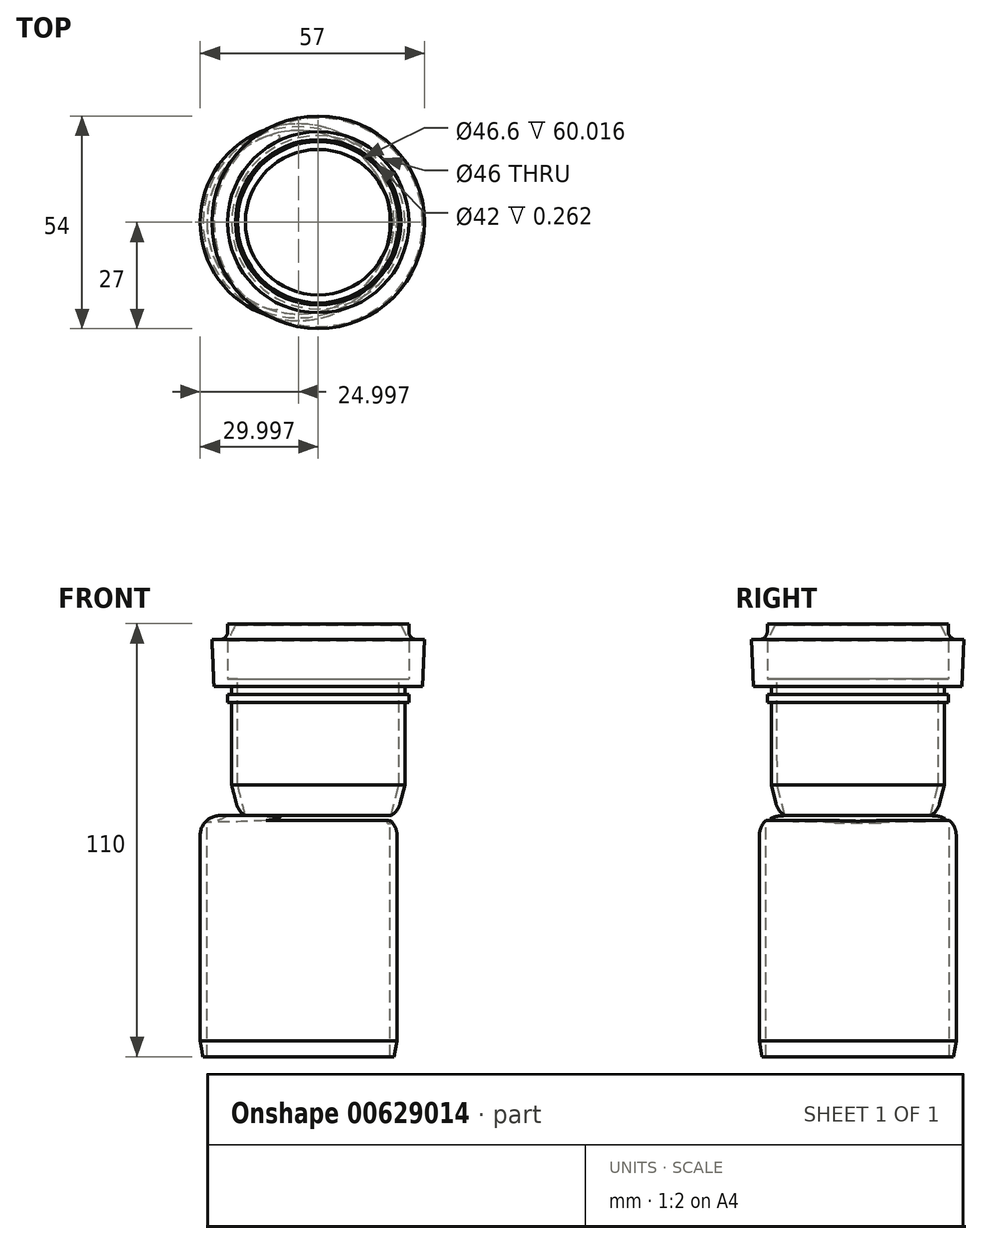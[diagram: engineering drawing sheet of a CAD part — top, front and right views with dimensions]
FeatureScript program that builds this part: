
annotation { "Feature Type Name" : "Feature", "Feature Type Description" : "" }
export const myFeature = defineFeature(function(context is Context, id is Id, definition is map)
    precondition{}
    {
        {
            var Q0;
            Q0=qCreatedBy(makeId("Front.planeOp"),FACE);
            var sketch = newSketch(context, id + "F0", { "sketchPlane" : qUnion([Q0])});
            skLineSegment(sketch, "E0", {"start": v(21.37, -67.8) * mm, "end": v(21.37, 7.5) * mm});
            skLineSegment(sketch, "E1", {"start": v(-0.63, -1.77) * mm, "end": v(-0.63, -22.77) * mm});
            skLineSegment(sketch, "E2", {"start": v(-0.63, -22.77) * mm, "end": v(1.37, -30.52) * mm});
            skLineSegment(sketch, "E3", {"start": v(-0.63, -1.77) * mm, "end": v(-1.63, -1.77) * mm});
            skLineSegment(sketch, "E4", {"start": v(-1.63, -1.77) * mm, "end": v(-1.63, 0.23) * mm});
            skLineSegment(sketch, "E5", {"start": v(-1.63, 0.23) * mm, "end": v(-0.63, 0.23) * mm});
            skLineSegment(sketch, "E6", {"start": v(-0.63, 0.23) * mm, "end": v(-0.63, 2.23) * mm});
            skLineSegment(sketch, "E7", {"start": v(-0.63, 2.23) * mm, "end": v(-5.13, 2.23) * mm});
            skLineSegment(sketch, "E8", {"start": v(-5.13, 2.23) * mm, "end": v(-5.63, 14.22) * mm});
            skLineSegment(sketch, "E9", {"start": v(-5.63, 14.22) * mm, "end": v(-3.63, 14.22) * mm});
            skLineSegment(sketch, "E10", {"start": v(-1.63, 16.22) * mm, "end": v(-1.63, 18.22) * mm});
            skLineSegment(sketch, "E11", {"start": v(-1.63, 18.22) * mm, "end": v(0.37, 18.22) * mm});
            skLineSegment(sketch, "E12", {"start": v(-1.63, 4.23) * mm, "end": v(-1.63, 13.9) * mm});
            skLineSegment(sketch, "E13", {"start": v(-1.63, 4.23) * mm, "end": v(0.87, 4.24) * mm});
            skPoint(sketch, "E14.visualSharp", {"position": v(-1.63, 14.22) * mm});
            skArc(sketch, "E14.filletArc", {"start": v(-3.63, 14.22) * mm, "mid": v(-2.22, 14.8) * mm, "end": v(-1.63, 16.22) * mm});
            skLineSegment(sketch, "E15", {"start": v(1.37, -30.52) * mm, "end": v(2.87, -30.52) * mm});
            skLineSegment(sketch, "E16", {"start": v(0.89, -22.73) * mm, "end": v(0.87, 4.24) * mm});
            skLineSegment(sketch, "E17", {"start": v(2.87, -30.52) * mm, "end": v(0.89, -22.73) * mm});
            skLineSegment(sketch, "E18", {"start": v(0.37, 18.22) * mm, "end": v(0.37, 17.95) * mm});
            skLineSegment(sketch, "E19", {"start": v(0.37, 17.95) * mm, "end": v(-1.63, 13.9) * mm});
            skSolve(sketch);
        }
        {
            var Q0;
            Q0=makeQuery(id+"F0.imprint","IMPRINT",FACE,{"disambiguationData":[TD([[makeQuery(id+"F0.imprint","IMPRINT",EDGE,{"derivedFrom":sQuery(id+"F0.wireOp",EDGE,"E1")}),1.0]])]});
            var Q1;
            Q1=sQuery(id+"F0.wireOp",EDGE,"E0");
            revolve(context, id + "F1", {"entities" : qUnion([Q0]), "axis" : qUnion([Q1]), "revolveType" : RevolveType.FULL});
        }
        {
            var Q0;
            Q0=makeQuery(id+"F1.opRevolve","SWEPT_FACE",FACE,{"disambiguationData":[OSD([sQuery(id+"F0.wireOp",EDGE,"E15")])]});
            cPlane(context, id + "F2", {"entities" : qUnion([Q0]), "cplaneType" : CPlaneType.OFFSET, "offset" : 0 * mm, "width" : 150 * mm, "height" : 150 * mm});
        }
        {
            var Q0;
            Q0=qCreatedBy(id+"F2.planeOp",FACE);
            var sketch = newSketch(context, id + "F3", { "sketchPlane" : qUnion([Q0])});
            skPoint(sketch, "E20", {"position": v(16.37, 0) * mm});
            skCircle(sketch, "E21", {"center": v(16.37, 0) * mm, "radius": 25 * mm});
            skSolve(sketch);
        }
        {
            var Q0;
            Q0 = qSketchRegion(id + "F3", true);
            extrude(context, id + "F4", {"entities" : qUnion([Q0]), "depth" : 61.26 * mm, "offsetDistance" : 25 * mm});
        }
        {
            var Q0;
            Q0=makeQuery(id+"F4.opExtrude","CAP_FACE",FACE,{"disambiguationData":[OSD([sQuery(id+"F3.wireOp",EDGE,"E21")])],"isStart":false});
            shell(context, id + "F5", {"entities" : qUnion([Q0]), "thickness" : 1.7 * mm});
        }
        {
            var Q0;
            Q0=qCreatedBy(id+"F2.planeOp",FACE);
            var sketch = newSketch(context, id + "F6", { "sketchPlane" : qUnion([Q0])});
            skCircle(sketch, "E22.0", {"center": v(21.37, 0) * mm, "radius": 18.5 * mm});
            skSolve(sketch);
        }
        {
            var Q0;
            Q0 = qSketchRegion(id + "F6", true);
            extrude(context, id + "F7", {"entities" : qUnion([Q0]), "operationType" : NewBodyOperationType.REMOVE, "depth" : 2 * mm, "offsetDistance" : 25 * mm});
        }
        {
            var Q0;
            Q0=makeQuery(id+"F4.opExtrude","CAP_EDGE",EDGE,{"disambiguationData":[OSD([sQuery(id+"F3.wireOp",EDGE,"E21")])],"isStart":false});
            chamfer(context, id + "F8", {"entities" : qUnion([Q0]), "chamferType" : ChamferType.OFFSET_ANGLE, "width" : 4 * mm, "oppositeDirection" : true, "angle" : 10 * degree, "tangentPropagation" : true});
        }
        {
            var Q0;
            Q0=makeQuery(id+"F1.opRevolve","SWEPT_EDGE",EDGE,{"disambiguationData":[OSD([sQuery(id+"F0.wireOp",EDGE,"E2"),sQuery(id+"F0.wireOp",EDGE,"E15")])]});
            fillet(context, id + "F9", {"entities" : qUnion([Q0]), "radius" : 5 * mm, "tangentPropagation" : true, "allowEdgeOverflow" : false});
        }
        {
            var Q0;
            Q0=makeQuery(id+"F4.opExtrude","CAP_EDGE",EDGE,{"disambiguationData":[OSD([sQuery(id+"F3.wireOp",EDGE,"E21")])],"isStart":true});
            fillet(context, id + "F10", {"entities" : qUnion([Q0]), "radius" : 5 * mm, "tangentPropagation" : true, "allowEdgeOverflow" : false});
        }
        {
            var Q0;
            {var subQ0=sQuery(id+"F3.wireOp",EDGE,"E21");Q0=makeQuery(id+"F7.boolean.opBoolean","INTERSECT",EDGE,{"derivedFrom":[makeQuery(id+"F5.opShell","OFFSET_FACE",FACE,{"disambiguationData":[OSD([subQ0]),TDD([makeQuery(id+"F4.opExtrude","CAP_FACE",FACE,{"disambiguationData":[OSD([subQ0])],"isStart":true})])]}),makeQuery(id+"F7.opExtrude","SWEPT_FACE",FACE,{"disambiguationData":[OSD([sQuery(id+"F6.wireOp",EDGE,"E22.0")])]})]});}
            fillet(context, id + "F11", {"entities" : qUnion([Q0]), "radius" : 10 * mm, "tangentPropagation" : true, "allowEdgeOverflow" : false});
        }
    });
